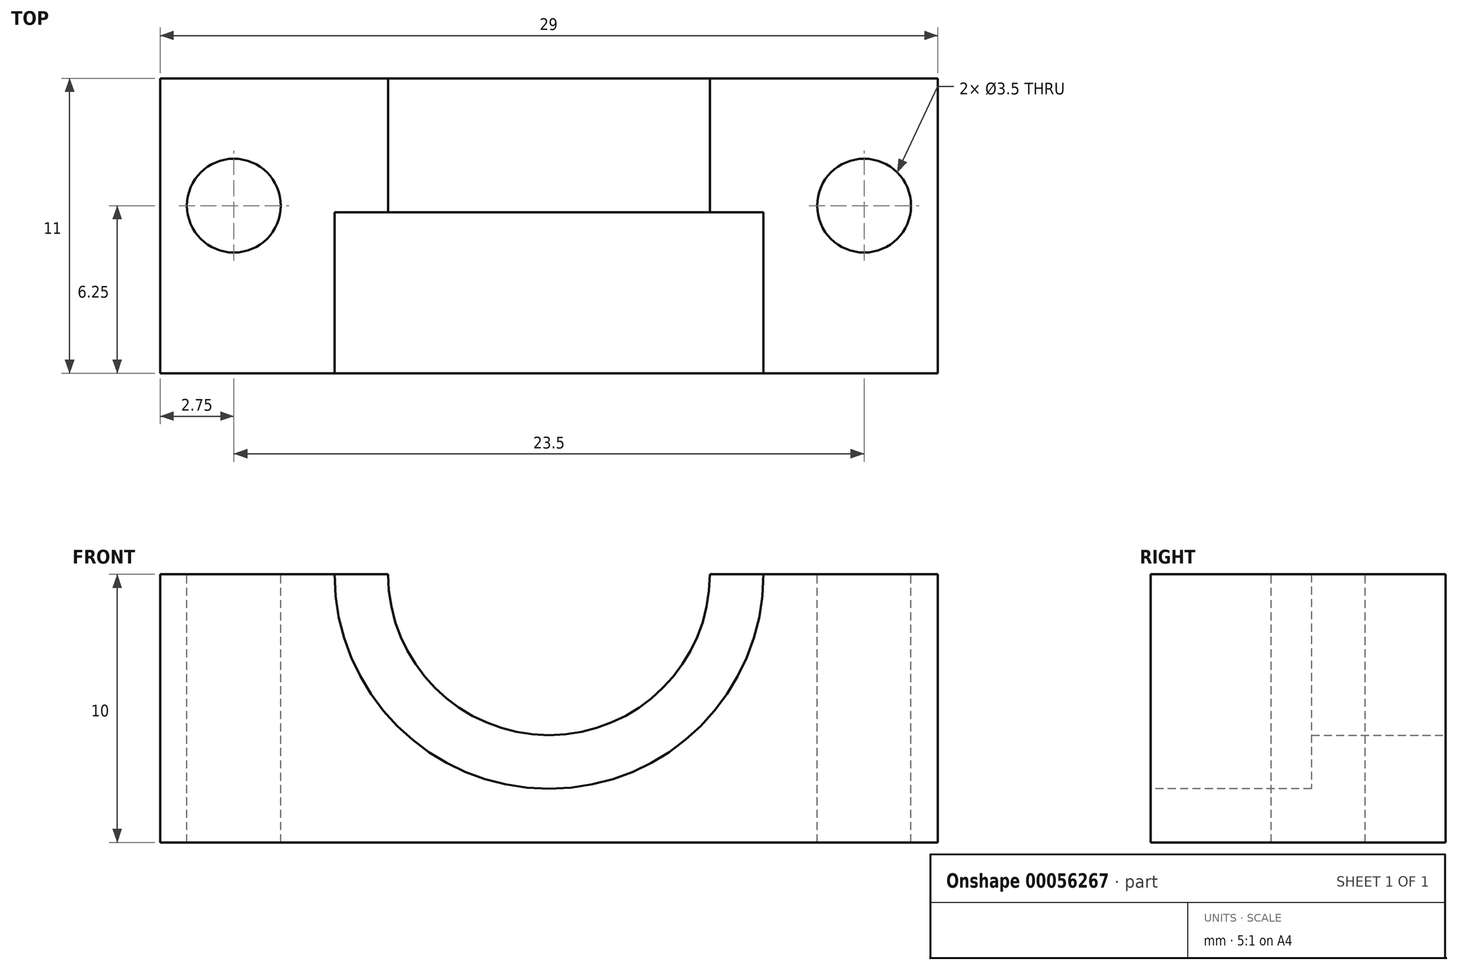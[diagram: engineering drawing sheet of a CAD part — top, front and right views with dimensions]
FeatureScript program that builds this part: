
annotation { "Feature Type Name" : "Feature", "Feature Type Description" : "" }
export const myFeature = defineFeature(function(context is Context, id is Id, definition is map)
    precondition{}
    {
        {
            var Q0;
            Q0=qCreatedBy(makeId("Top.planeOp"),FACE);
            var sketch = newSketch(context, id + "F0", { "sketchPlane" : qUnion([Q0])});
            skLineSegment(sketch, "E0.bottom", {"start": v(0, 0) * mm, "end": v(25, 0) * mm});
            skLineSegment(sketch, "E0.top", {"start": v(0, 11) * mm, "end": v(25, 11) * mm});
            skLineSegment(sketch, "E0.left", {"start": v(0, 0) * mm, "end": v(0, 11) * mm});
            skLineSegment(sketch, "E0.right", {"start": v(25, 0) * mm, "end": v(25, 11) * mm});
            skSolve(sketch);
        }
        {
            var Q0;
            Q0=qSketchRegion(id+"F0",true);
            extrude(context, id + "F1", {"entities" : qUnion([Q0]), "depth" : 10 * mm});
        }
        {
            var Q0;
            Q0=makeQuery(id+"F1.opExtrude","SWEPT_FACE",FACE,{"disambiguationData":[OSD([sQuery(id+"F0.wireOp",EDGE,"E0.bottom")])]});
            var sketch = newSketch(context, id + "F2", { "sketchPlane" : qUnion([Q0])});
            skCircle(sketch, "E1", {"center": v(12.5, 10) * mm, "radius": 8 * mm});
            skSolve(sketch);
        }
        {
            var Q0;
            Q0=qSketchRegion(id+"F2",true);
            extrude(context, id + "F3", {"entities" : qUnion([Q0]), "operationType" : NewBodyOperationType.REMOVE, "oppositeDirection" : true, "depth" : 6 * mm});
        }
        {
            var Q0;
            Q0=makeQuery(id+"F1.opExtrude","SWEPT_FACE",FACE,{"disambiguationData":[OSD([sQuery(id+"F0.wireOp",EDGE,"E0.top")])]});
            var sketch = newSketch(context, id + "F4", { "sketchPlane" : qUnion([Q0])});
            skCircle(sketch, "E2", {"center": v(-12.5, 10) * mm, "radius": 6 * mm});
            skSolve(sketch);
        }
        {
            var Q0;
            Q0=qSketchRegion(id+"F4",true);
            extrude(context, id + "F5", {"entities" : qUnion([Q0]), "operationType" : NewBodyOperationType.REMOVE, "oppositeDirection" : true, "depth" : 6 * mm});
        }
        {
            var Q0;
            Q0=makeQuery(id+"F1.opExtrude","SWEPT_FACE",FACE,{"disambiguationData":[OSD([sQuery(id+"F0.wireOp",EDGE,"E0.left")])]});
            var sketch = newSketch(context, id + "F6", { "sketchPlane" : qUnion([Q0])});
            skLineSegment(sketch, "E3.bottom", {"start": v(-11, 0) * mm, "end": v(0, 0) * mm});
            skLineSegment(sketch, "E3.top", {"start": v(-11, 10) * mm, "end": v(0, 10) * mm});
            skLineSegment(sketch, "E3.left", {"start": v(-11, 0) * mm, "end": v(-11, 10) * mm});
            skLineSegment(sketch, "E3.right", {"start": v(0, 0) * mm, "end": v(0, 10) * mm});
            skSolve(sketch);
        }
        {
            var Q0;
            Q0=qSketchRegion(id+"F6",true);
            extrude(context, id + "F7", {"entities" : qUnion([Q0]), "operationType" : NewBodyOperationType.ADD, "depth" : 2 * mm});
        }
        {
            var Q0;
            Q0=makeQuery(id+"F1.opExtrude","SWEPT_FACE",FACE,{"disambiguationData":[OSD([sQuery(id+"F0.wireOp",EDGE,"E0.right")])]});
            var sketch = newSketch(context, id + "F8", { "sketchPlane" : qUnion([Q0])});
            skLineSegment(sketch, "E4.bottom", {"start": v(11, 10) * mm, "end": v(0, 10) * mm});
            skLineSegment(sketch, "E4.top", {"start": v(11, 0) * mm, "end": v(0, 0) * mm});
            skLineSegment(sketch, "E4.left", {"start": v(11, 10) * mm, "end": v(11, 0) * mm});
            skLineSegment(sketch, "E4.right", {"start": v(0, 10) * mm, "end": v(0, 0) * mm});
            skSolve(sketch);
        }
        {
            var Q0;
            Q0=qSketchRegion(id+"F8",true);
            extrude(context, id + "F9", {"entities" : qUnion([Q0]), "operationType" : NewBodyOperationType.ADD, "depth" : 2 * mm});
        }
        {
            var Q0;
            {var subQ0=sQuery(id+"F0.wireOp",EDGE,"E0.bottom");var subQ1=sQuery(id+"F0.wireOp",EDGE,"E0.top");var subQ2=sQuery(id+"F0.wireOp",EDGE,"E0.left");Q0=makeQuery(id+"F5.boolean.opBoolean","SPLIT",FACE,{"disambiguationData":[TD([makeQuery(id+"F1.opExtrude","SWEPT_FACE",FACE,{"disambiguationData":[OSD([subQ2])]})])],"derivedFrom":makeQuery(id+"F1.opExtrude","CAP_FACE",FACE,{"disambiguationData":[OSD([subQ0,subQ1,subQ2,sQuery(id+"F0.wireOp",EDGE,"E0.right")])],"isStart":false})});}
            var sketch = newSketch(context, id + "F10", { "sketchPlane" : qUnion([Q0])});
            skCircle(sketch, "E5", {"center": v(0.75, 6.25) * mm, "radius": 1.75 * mm});
            skCircle(sketch, "E6", {"center": v(24.25, 6.25) * mm, "radius": 1.75 * mm});
            skSolve(sketch);
        }
        {
            var Q0;
            Q0=qSketchRegion(id+"F10",true);
            extrude(context, id + "F11", {"entities" : qUnion([Q0]), "operationType" : NewBodyOperationType.REMOVE, "oppositeDirection" : true, "depth" : 25 * mm});
        }
    });
